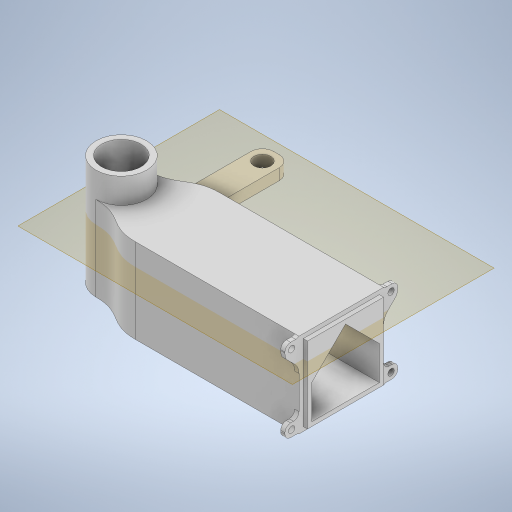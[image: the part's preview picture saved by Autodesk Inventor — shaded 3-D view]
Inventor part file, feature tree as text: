
AUTODESK INVENTOR PART (.ipt)
format: ipt  version: 2024 (Build 280153000, 153)  size: 521,728 bytes
history: native  units: in
note: dims shown in document units (in); Inventor stores cm internally (conversion verified against a paired STEP export)
features: extrude x8, sketch x7, fillet x4, projected_geometry x3, plane x2, hole x1, chamfer x1
ambient origin geometry x8: Origin, YZ Plane, XZ Plane, XY Plane, X Axis, Y Axis, Z Axis, Center Point
bodies: Solid1 (feature_tree)
feature tree (26):
  extrude  "Extrusion1"  Depth=0.0787in
  plane  "Work Plane1"
  extrude  "Extrusion2"  Depth=0.374in
  sketch  "Sketch4"  dims[d5=1.1811in d6=0.1181in]
  extrude  "Extrusion4"  Depth=0.1181in
  hole  "Hole2"  [1 undecoded]
  sketch  "Sketch9"  dims[d10=0.4724in d11=0.1181in]
  extrude  "Extrusion7"  Depth=0.1181in
  extrude  "Extrusion8"  Depth=1.1811in
  extrude  "Extrusion9"  Depth=0.1575in TaperAngle=0.0deg
  extrude  "Extrusion3"  Depth=0.1575in
  fillet  "Fillet1"  Radius=1.1811in
  chamfer  "Chamfer1"  Distance=1.1811in
  fillet  "Fillet2"  Radius=0.0591in
  plane  "Work Plane3"
  extrude  "Extrusion10"  Depth=0.1575in TaperAngle=0.0deg
  fillet  "Fillet3"  Radius=0.0591in
  fillet  "Fillet4"  Radius=0.748in
  sketch  "Sketch1"  dims[d0=0.7087in d1=0.0787in]
  sketch  "Sketch2"  dims[d2=0.4724in d3=0.0in d4=0.374in]
  projected_geometry  "Projected Loop1"
  sketch  "Sketch8"  dims[d7=0.1181in d9=0.9449in]
  projected_geometry  "Projected Loop5"
  sketch  "Sketch11"  dims[d12=0.1181in d13=1.1811in]
  sketch  "Sketch12"  dims[d20=0.1181in d23=2.7559in d24=0.0in d25=0.0886in d26=1.1811in d27=1.1811in d35=0.0591in d36=0.2362in d37=0.0in d38=0.0591in d39=0.0in d40=0.748in d41=0.0in d53=0.5906in d54=0.1033in d55=0.1033in d56=0.1033in d57=0.1033in d58=0.1033in d60=0.1033in d61=0.1033in d62=0.5906in d63=0.2362in d64=0.1575in d65=0.0787in d66=90.0deg d67=0.3937in d68=0.8108in d69=0.7874in d70=0.0787in d71=0.0787in d72=0.0in d73=0.0in d74=1.1811in d75=0.0in d76=0.1033in d77=0.1033in d78=0.1033in d79=0.1033in d80=0.1772in d82=0.1772in d86=0.0591in d87=0.0in d91=0.0787in d92=0.0148in d93=0.0886in d94=0.1969in d95=0.1969in d99=0.0148in d100=0.1772in d101=0.0787in d102=45.0deg d103=0.1969in d104=0.4724in d105=0.4724in d106=0.4724in d107=0.2362in d108=0.3937in d109=1.5748in d110=0.3937in d111=0.1969in d113=0.1969in d114=0.1575in d115=0.0in d116=0.1969in d117=0.1575in d119=-0.187in]
  projected_geometry  "Projected Loop6"
note: 1 required parameter value undecoded (feature->parameter linkage not recoverable at this tier; creation-order binding heuristic only, values carry confidence <= 0.55)
